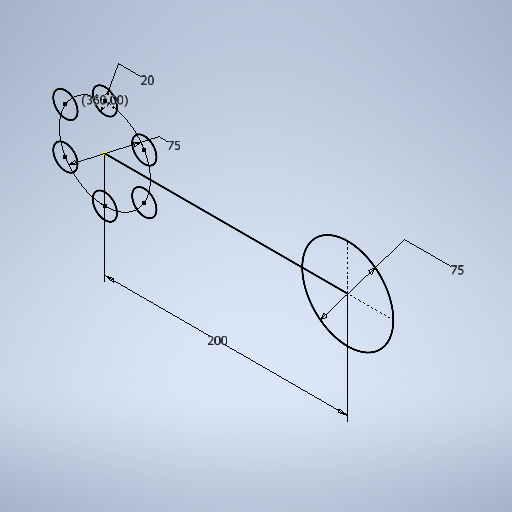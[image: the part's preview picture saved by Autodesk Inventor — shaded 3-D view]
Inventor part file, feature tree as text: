
AUTODESK INVENTOR PART (.ipt)
format: ipt  version: 2025.2 (Build 292293000, 293)  size: 275,968 bytes
history: native  units: mm
features: sketch x5
ambient origin geometry x8: Origin, YZ Plane, XZ Plane, XY Plane, X Axis, Y Axis, Z Axis, Center Point
feature tree (5):
  sketch  "Esboço Suave"  dims[d1=50.0mm]
  sketch  "Esboço Simetria"  dims[d2=20.0mm]
  sketch  "Esboço Igual"  dims[d3=75.0mm]
  sketch  "Esboço Circular"  dims[d4=60.0mm d6=360.0deg d8=200.0mm d9=75.0mm]
  sketch  "Esboço - Padrão circular1"  dims[d0=20.0mm]
